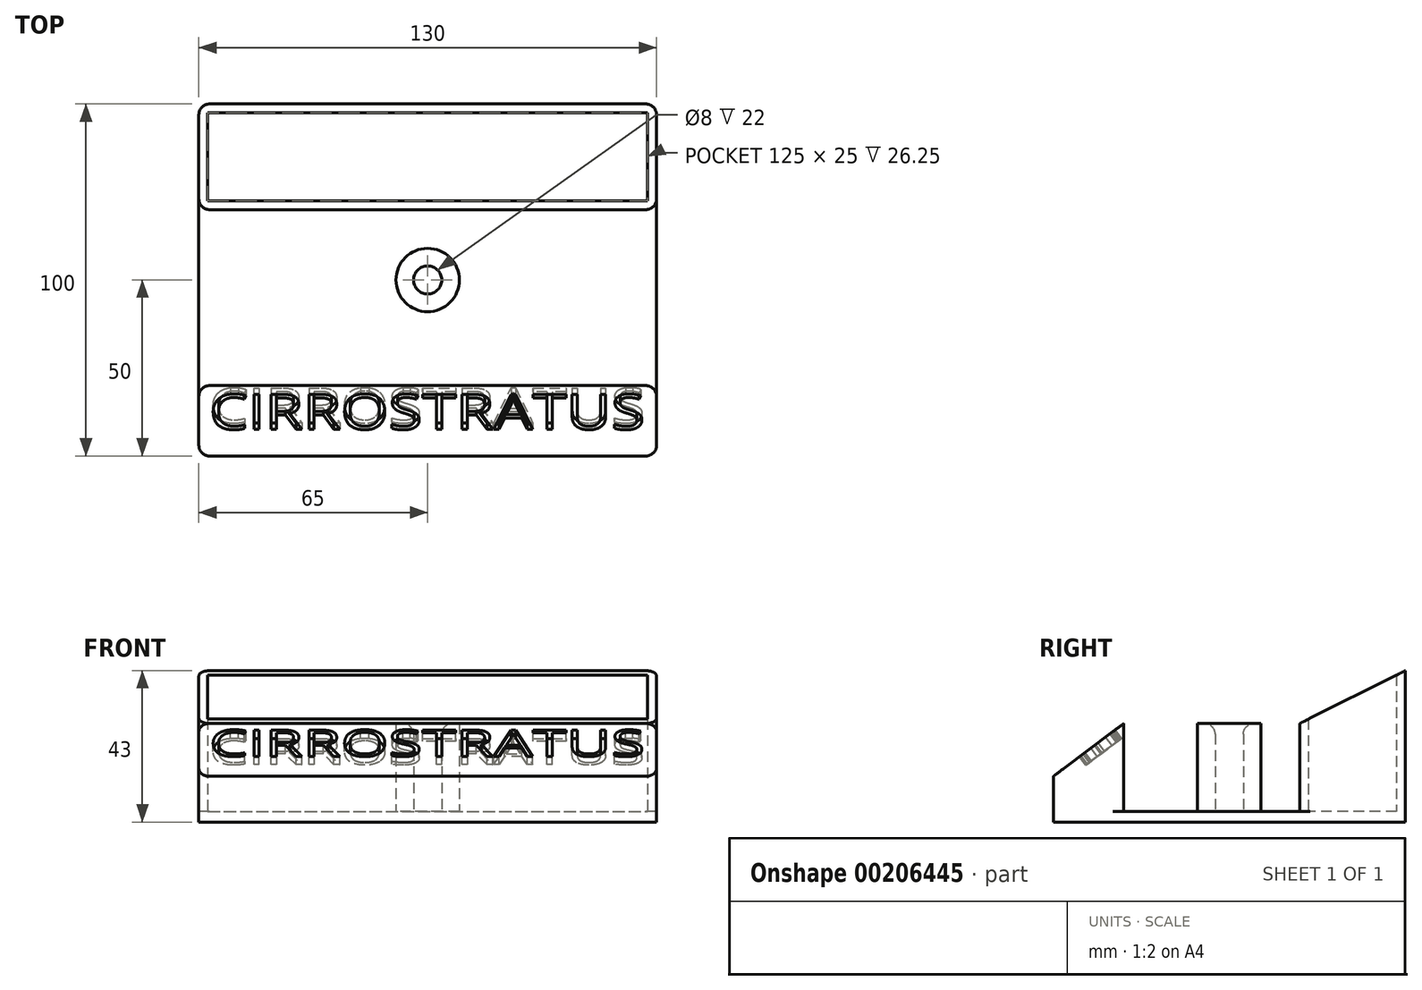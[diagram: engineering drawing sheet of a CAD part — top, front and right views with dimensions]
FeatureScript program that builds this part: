
annotation { "Feature Type Name" : "Feature", "Feature Type Description" : "" }
export const myFeature = defineFeature(function(context is Context, id is Id, definition is map)
    precondition{}
    {
        {
            var Q0;
            Q0=qCreatedBy(makeId("Top.planeOp"),FACE);
            var sketch = newSketch(context, id + "F0", { "sketchPlane" : qUnion([Q0])});
            skLineSegment(sketch, "E0.bottom", {"start": v(-65, 100) * mm, "end": v(65, 100) * mm});
            skLineSegment(sketch, "E0.top", {"start": v(-65, 0) * mm, "end": v(65, 0) * mm});
            skLineSegment(sketch, "E0.left", {"start": v(65, 100) * mm, "end": v(65, 0) * mm});
            skLineSegment(sketch, "E0.right", {"start": v(-65, 100) * mm, "end": v(-65, 0) * mm});
            skSolve(sketch);
        }
        {
            var Q0;
            Q0=makeQuery(id+"F0.imprint","IMPRINT",FACE,{"disambiguationData":[TD([[makeQuery(id+"F0.imprint","IMPRINT",EDGE,{"derivedFrom":sQuery(id+"F0.wireOp",EDGE,"E0.bottom")}),-1.0]])]});
            extrude(context, id + "F1", {"entities" : qUnion([Q0]), "depth" : 3 * mm});
        }
        {
            var Q0;
            Q0=makeQuery(id+"F1.opExtrude","CAP_FACE",FACE,{"disambiguationData":[OSD([sQuery(id+"F0.wireOp",EDGE,"E0.bottom"),sQuery(id+"F0.wireOp",EDGE,"E0.top"),sQuery(id+"F0.wireOp",EDGE,"E0.left"),sQuery(id+"F0.wireOp",EDGE,"E0.right")])],"isStart":false});
            var sketch = newSketch(context, id + "F2", { "sketchPlane" : qUnion([Q0])});
            skLineSegment(sketch, "E1", {"start": v(0, 0) * mm, "end": v(0, 100) * mm, "construction": true});
            skCircle(sketch, "E2", {"center": v(0, 50) * mm, "radius": 9 * mm});
            skCircle(sketch, "E3", {"center": v(0, 50) * mm, "radius": 4 * mm});
            skLineSegment(sketch, "E4.bottom", {"start": v(-65, 0) * mm, "end": v(65, 0) * mm});
            skLineSegment(sketch, "E4.top", {"start": v(-65, 20) * mm, "end": v(65, 20) * mm});
            skLineSegment(sketch, "E4.left", {"start": v(-65, 0) * mm, "end": v(-65, 20) * mm});
            skLineSegment(sketch, "E4.right", {"start": v(65, 0) * mm, "end": v(65, 20) * mm});
            skLineSegment(sketch, "E5.bottom", {"start": v(-65, 100) * mm, "end": v(65, 100) * mm});
            skLineSegment(sketch, "E5.top", {"start": v(-65, 70) * mm, "end": v(65, 70) * mm});
            skLineSegment(sketch, "E5.left", {"start": v(-65, 100) * mm, "end": v(-65, 70) * mm});
            skLineSegment(sketch, "E5.right", {"start": v(65, 100) * mm, "end": v(65, 70) * mm});
            skLineSegment(sketch, "E6.0", {"start": v(62.5, 97.5) * mm, "end": v(62.5, 72.5) * mm});
            skLineSegment(sketch, "E6.1", {"start": v(-62.5, 97.5) * mm, "end": v(62.5, 97.5) * mm});
            skLineSegment(sketch, "E6.2", {"start": v(-62.5, 97.5) * mm, "end": v(-62.5, 72.5) * mm});
            skLineSegment(sketch, "E6.3", {"start": v(-62.5, 72.5) * mm, "end": v(62.5, 72.5) * mm});
            skSolve(sketch);
        }
        {
            var Q0;
            Q0=makeQuery(id+"F2.imprint","IMPRINT",FACE,{"disambiguationData":[TD([[makeQuery(id+"F2.imprint","IMPRINT",EDGE,{"derivedFrom":sQuery(id+"F2.wireOp",EDGE,"E5.bottom")}),-1.0]])]});
            extrude(context, id + "F3", {"entities" : qUnion([Q0]), "operationType" : NewBodyOperationType.ADD, "depth" : 40 * mm});
        }
        {
            var Q0;
            Q0=makeQuery(id+"F2.imprint","IMPRINT",FACE,{"disambiguationData":[TD([[makeQuery(id+"F2.imprint","IMPRINT",EDGE,{"derivedFrom":sQuery(id+"F2.wireOp",EDGE,"E2")}),1.0]])]});
            var Q1;
            Q1=makeQuery(id+"F2.imprint","IMPRINT",FACE,{"disambiguationData":[TD([[makeQuery(id+"F2.imprint","IMPRINT",EDGE,{"derivedFrom":sQuery(id+"F2.wireOp",EDGE,"E4.bottom")}),1.0]])]});
            extrude(context, id + "F4", {"entities" : qUnion([Q0, Q1]), "operationType" : NewBodyOperationType.ADD, "depth" : 25 * mm});
        }
        {
            var Q0;
            Q0=makeQuery(id+"F4.opExtrude","CAP_EDGE",EDGE,{"disambiguationData":[OSD([sQuery(id+"F2.wireOp",EDGE,"E4.bottom")])],"isStart":false});
            chamfer(context, id + "F5", {"entities" : qUnion([Q0]), "chamferType" : ChamferType.TWO_OFFSETS, "width1" : 20 * mm, "oppositeDirection" : false, "width2" : 15 * mm, "tangentPropagation" : true});
        }
        {
            var Q0;
            Q0=makeQuery(id+"F3.opExtrude","CAP_EDGE",EDGE,{"disambiguationData":[OSD([sQuery(id+"F2.wireOp",EDGE,"E5.top")])],"isStart":false});
            chamfer(context, id + "F6", {"entities" : qUnion([Q0]), "chamferType" : ChamferType.TWO_OFFSETS, "width1" : 30 * mm, "oppositeDirection" : false, "width2" : 15 * mm, "tangentPropagation" : true});
        }
        {
            var Q0;
            Q0=makeQuery(id+"F3.boolean.opBoolean","MERGE",EDGE,{"derivedFrom":[makeQuery(id+"F1.opExtrude","SWEPT_EDGE",EDGE,{"disambiguationData":[OSD([sQuery(id+"F0.wireOp",EDGE,"E0.bottom"),sQuery(id+"F0.wireOp",EDGE,"E0.right")])]}),makeQuery(id+"F3.opExtrude","SWEPT_EDGE",EDGE,{"disambiguationData":[OSD([sQuery(id+"F2.wireOp",EDGE,"E5.bottom"),sQuery(id+"F2.wireOp",EDGE,"E5.left")])]})]});
            var Q1;
            Q1=makeQuery(id+"F3.opExtrude","SWEPT_EDGE",EDGE,{"disambiguationData":[OSD([sQuery(id+"F0.wireOp",EDGE,"E0.right"),sQuery(id+"F2.wireOp",EDGE,"E5.top"),sQuery(id+"F2.wireOp",EDGE,"E5.left")])]});
            var Q2;
            Q2=makeQuery(id+"F3.opExtrude","SWEPT_EDGE",EDGE,{"disambiguationData":[OSD([sQuery(id+"F0.wireOp",EDGE,"E0.left"),sQuery(id+"F2.wireOp",EDGE,"E5.top"),sQuery(id+"F2.wireOp",EDGE,"E5.right")])]});
            var Q3;
            Q3=makeQuery(id+"F4.boolean.opBoolean","MERGE",EDGE,{"derivedFrom":[makeQuery(id+"F1.opExtrude","SWEPT_EDGE",EDGE,{"disambiguationData":[OSD([sQuery(id+"F0.wireOp",EDGE,"E0.top"),sQuery(id+"F0.wireOp",EDGE,"E0.right")])]}),makeQuery(id+"F4.opExtrude","SWEPT_EDGE",EDGE,{"disambiguationData":[OSD([sQuery(id+"F2.wireOp",EDGE,"E4.bottom"),sQuery(id+"F2.wireOp",EDGE,"E4.left")])]})]});
            var Q4;
            Q4=makeQuery(id+"F3.boolean.opBoolean","MERGE",EDGE,{"derivedFrom":[makeQuery(id+"F1.opExtrude","SWEPT_EDGE",EDGE,{"disambiguationData":[OSD([sQuery(id+"F0.wireOp",EDGE,"E0.bottom"),sQuery(id+"F0.wireOp",EDGE,"E0.left")])]}),makeQuery(id+"F3.opExtrude","SWEPT_EDGE",EDGE,{"disambiguationData":[OSD([sQuery(id+"F2.wireOp",EDGE,"E5.bottom"),sQuery(id+"F2.wireOp",EDGE,"E5.right")])]})]});
            var Q5;
            Q5=makeQuery(id+"F4.boolean.opBoolean","MERGE",EDGE,{"derivedFrom":[makeQuery(id+"F1.opExtrude","SWEPT_EDGE",EDGE,{"disambiguationData":[OSD([sQuery(id+"F0.wireOp",EDGE,"E0.top"),sQuery(id+"F0.wireOp",EDGE,"E0.left")])]}),makeQuery(id+"F4.opExtrude","SWEPT_EDGE",EDGE,{"disambiguationData":[OSD([sQuery(id+"F2.wireOp",EDGE,"E4.bottom"),sQuery(id+"F2.wireOp",EDGE,"E4.right")])]})]});
            var Q6;
            Q6=makeQuery(id+"F4.opExtrude","SWEPT_EDGE",EDGE,{"disambiguationData":[OSD([sQuery(id+"F0.wireOp",EDGE,"E0.left"),sQuery(id+"F2.wireOp",EDGE,"E4.top"),sQuery(id+"F2.wireOp",EDGE,"E4.right")])]});
            var Q7;
            Q7=makeQuery(id+"F4.opExtrude","SWEPT_EDGE",EDGE,{"disambiguationData":[OSD([sQuery(id+"F0.wireOp",EDGE,"E0.right"),sQuery(id+"F2.wireOp",EDGE,"E4.top"),sQuery(id+"F2.wireOp",EDGE,"E4.left")])]});
            var Q8;
            Q8=makeQuery(id+"F4.opExtrude","CAP_EDGE",EDGE,{"disambiguationData":[OSD([sQuery(id+"F2.wireOp",EDGE,"E3")])],"isStart":false});
            fillet(context, id + "F7", {"entities" : qUnion([Q0, Q1, Q2, Q3, Q4, Q5, Q6, Q7, Q8]), "radius" : 3 * mm, "tangentPropagation" : true, "allowEdgeOverflow" : false});
        }
        {
            var Q0;
            Q0=makeQuery(id+"F5.opChamfer","BLEND_FACE",FACE,{"disambiguationData":[OSD([sQuery(id+"F2.wireOp",EDGE,"E4.bottom")])]});
            var sketch = newSketch(context, id + "F8", { "sketchPlane" : qUnion([Q0])});
            skLineSegment(sketch, "E7.0", {"start": v(62, 10.8) * mm, "end": v(-62, 10.8) * mm});
            skLineSegment(sketch, "E8.0", {"start": v(-62, 29.8) * mm, "end": v(62, 29.8) * mm});
            skText(sketch, "E9", { "text": "CIRROSTRATUS", "fontName": "OpenSans-Regular.ttf"});
            skLineSegment(sketch, "E10", {"start": v(-62, 10.8) * mm, "end": v(-62, 47.82) * mm});
            skLineSegment(sketch, "E11", {"start": v(62, 10.8) * mm, "end": v(62, 49.07) * mm});
            skPoint(sketch, "E11.endSnap0", {"position": v(62, 15.3) * mm});
            const initialGuessF8  = {"E9": [-0.062, 0.01727, 1, 0, 0.01253]};
            skSetInitialGuess(sketch, initialGuessF8);
            skSolve(sketch);
        }
        {
            var Q0;
            Q0=makeQuery(id+"F8.imprint","IMPRINT",FACE,{"disambiguationData":[TD([[makeQuery(id+"F8.imprint","IMPRINT",EDGE,{"derivedFrom":sQuery(id+"F8.wireOp",EDGE,"E9.sketch_text.stroke-0")}),-1.0]])]});
            var Q1;
            Q1=makeQuery(id+"F8.imprint","IMPRINT",FACE,{"disambiguationData":[TD([[makeQuery(id+"F8.imprint","IMPRINT",EDGE,{"derivedFrom":sQuery(id+"F8.wireOp",EDGE,"E9.sketch_text.stroke-13")}),-1.0]])]});
            var Q2;
            Q2=makeQuery(id+"F8.imprint","IMPRINT",FACE,{"disambiguationData":[TD([[makeQuery(id+"F8.imprint","IMPRINT",EDGE,{"derivedFrom":sQuery(id+"F8.wireOp",EDGE,"E9.sketch_text.stroke-19")}),-1.0]])]});
            var Q3;
            Q3=makeQuery(id+"F8.imprint","IMPRINT",FACE,{"disambiguationData":[TD([[makeQuery(id+"F8.imprint","IMPRINT",EDGE,{"derivedFrom":sQuery(id+"F8.wireOp",EDGE,"E9.sketch_text.stroke-27")}),-1.0]])]});
            var Q4;
            Q4=makeQuery(id+"F8.imprint","IMPRINT",FACE,{"disambiguationData":[TD([[makeQuery(id+"F8.imprint","IMPRINT",EDGE,{"derivedFrom":sQuery(id+"F8.wireOp",EDGE,"E9.sketch_text.stroke-43")}),-1.0]])]});
            var Q5;
            Q5=makeQuery(id+"F8.imprint","IMPRINT",FACE,{"disambiguationData":[TD([[makeQuery(id+"F8.imprint","IMPRINT",EDGE,{"derivedFrom":sQuery(id+"F8.wireOp",EDGE,"E9.sketch_text.stroke-58")}),-1.0]])]});
            var Q6;
            Q6=makeQuery(id+"F8.imprint","IMPRINT",FACE,{"disambiguationData":[TD([[makeQuery(id+"F8.imprint","IMPRINT",EDGE,{"derivedFrom":sQuery(id+"F8.wireOp",EDGE,"E9.sketch_text.stroke-72")}),-1.0]])]});
            var Q7;
            Q7=makeQuery(id+"F8.imprint","IMPRINT",FACE,{"disambiguationData":[TD([[makeQuery(id+"F8.imprint","IMPRINT",EDGE,{"derivedFrom":sQuery(id+"F8.wireOp",EDGE,"E9.sketch_text.stroke-90")}),-1.0]])]});
            var Q8;
            Q8=makeQuery(id+"F8.imprint","IMPRINT",FACE,{"disambiguationData":[TD([[makeQuery(id+"F8.imprint","IMPRINT",EDGE,{"derivedFrom":sQuery(id+"F8.wireOp",EDGE,"E9.sketch_text.stroke-104")}),-1.0]])]});
            var Q9;
            Q9=makeQuery(id+"F8.imprint","IMPRINT",FACE,{"disambiguationData":[TD([[makeQuery(id+"F8.imprint","IMPRINT",EDGE,{"derivedFrom":sQuery(id+"F8.wireOp",EDGE,"E9.sketch_text.stroke-110")}),-1.0]])]});
            var Q10;
            Q10=makeQuery(id+"F8.imprint","IMPRINT",FACE,{"disambiguationData":[TD([[makeQuery(id+"F8.imprint","IMPRINT",EDGE,{"derivedFrom":sQuery(id+"F8.wireOp",EDGE,"E9.sketch_text.stroke-124")}),-1.0]])]});
            var Q11;
            Q11=makeQuery(id+"F8.imprint","IMPRINT",FACE,{"disambiguationData":[TD([[makeQuery(id+"F8.imprint","IMPRINT",EDGE,{"derivedFrom":sQuery(id+"F8.wireOp",EDGE,"E9.sketch_text.stroke-96")}),-1.0]])]});
            var Q12;
            Q12=makeQuery(id+"F8.imprint","IMPRINT",FACE,{"disambiguationData":[TD([[makeQuery(id+"F8.imprint","IMPRINT",EDGE,{"derivedFrom":sQuery(id+"F8.wireOp",EDGE,"E9.sketch_text.stroke-135")}),-1.0]])]});
            var Q13;
            Q13=makeQuery(id+"F8.imprint","IMPRINT",FACE,{"disambiguationData":[TD([[makeQuery(id+"F8.imprint","IMPRINT",EDGE,{"derivedFrom":sQuery(id+"F8.wireOp",EDGE,"E9.sketch_text.stroke-143")}),-1.0]])]});
            var Q14;
            Q14=makeQuery(id+"F8.imprint","IMPRINT",FACE,{"disambiguationData":[TD([[makeQuery(id+"F8.imprint","IMPRINT",EDGE,{"derivedFrom":sQuery(id+"F8.wireOp",EDGE,"E9.sketch_text.stroke-157")}),-1.0]])]});
            var Q15;
            Q15=makeQuery(id+"F8.imprint","IMPRINT",FACE,{"disambiguationData":[TD([[makeQuery(id+"F8.imprint","IMPRINT",EDGE,{"derivedFrom":sQuery(id+"F8.wireOp",EDGE,"E9.sketch_text.stroke-15")}),-1.0]])]});
            extrude(context, id + "F9", {"entities" : qUnion([Q0, Q1, Q2, Q3, Q4, Q5, Q6, Q7, Q8, Q9, Q10, Q11, Q12, Q13, Q14, Q15]), "operationType" : NewBodyOperationType.REMOVE, "oppositeDirection" : true, "depth" : 3 * mm});
        }
    });
